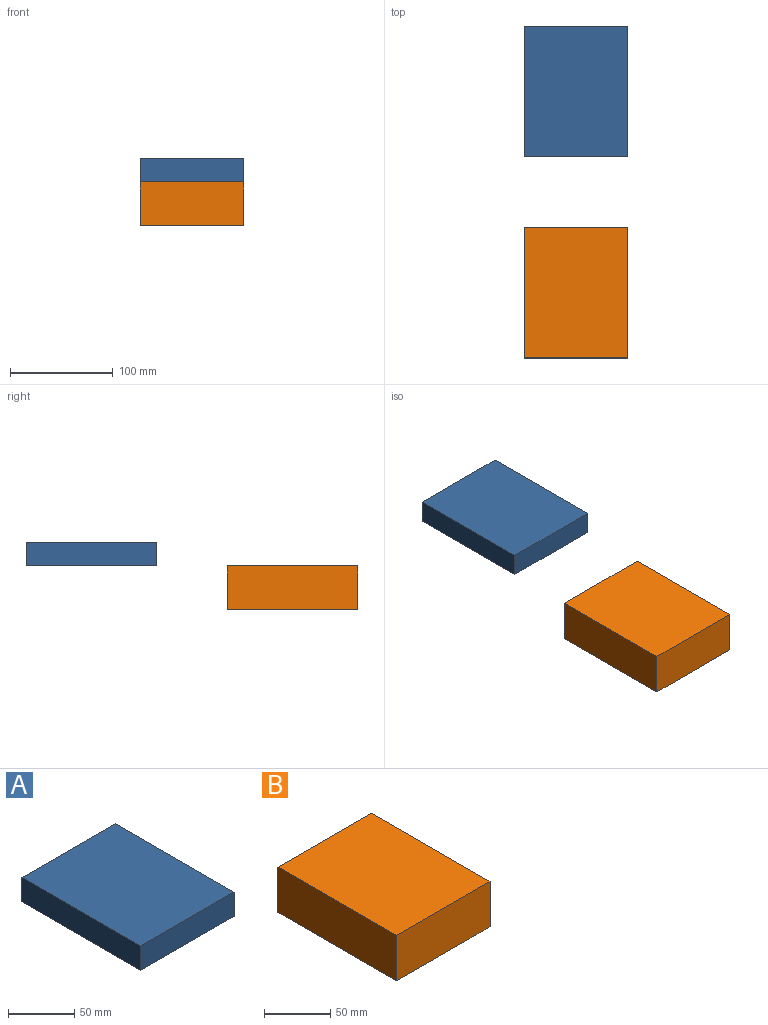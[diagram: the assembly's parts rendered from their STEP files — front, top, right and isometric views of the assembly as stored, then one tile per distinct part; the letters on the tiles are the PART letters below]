
ASSEMBLY  parts=2 mates=1
PART A: 6 faces, bbox 100.1x127x22.6 mm
  f0: plane 127x22.57mm, normal (-1,0,0), area 2865.9mm2, adj f1,f3,f4,f5
  f1: plane 127x100.07mm, normal (0,0,-1), area 12709mm2, adj f0,f2,f4,f5
  f2: plane 127x22.57mm, normal (1,0,0), area 2865.9mm2, adj f1,f3,f4,f5
  f3: plane 127x100.07mm, normal (0,0,1), area 12709mm2, adj f0,f2,f4,f5
  f4: plane 100.07x22.57mm, normal (0,-1,0), area 2258.2mm2, adj f0,f1,f2,f3
  f5: plane 100.07x22.57mm, normal (0,1,0), area 2258.2mm2, adj f0,f1,f2,f3
PART B: 6 faces, bbox 100.1x127x42.1 mm
  f0: plane 127x100.07mm, normal (0,0,1), area 12709mm2, adj f1,f3,f4,f5
  f1: plane 127x42.09mm, normal (-1,0,0), area 5345.9mm2, adj f0,f2,f4,f5
  f2: plane 127x100.07mm, normal (0,0,-1), area 12709mm2, adj f1,f3,f4,f5
  f3: plane 127x42.09mm, normal (1,0,0), area 5345.9mm2, adj f0,f2,f4,f5
  f4: plane 100.07x42.09mm, normal (0,-1,0), area 4212.4mm2, adj f0,f1,f2,f3
  f5: plane 100.07x42.09mm, normal (0,1,0), area 4212.4mm2, adj f0,f1,f2,f3
PLACE A t=(-50.04,258.83,0)mm
PLACE B t=(-50.04,63.5,0)mm
MATE slider A.f4 <-> B.f4  axis (0,-1,0) through (0,131.83,42.09)mm
